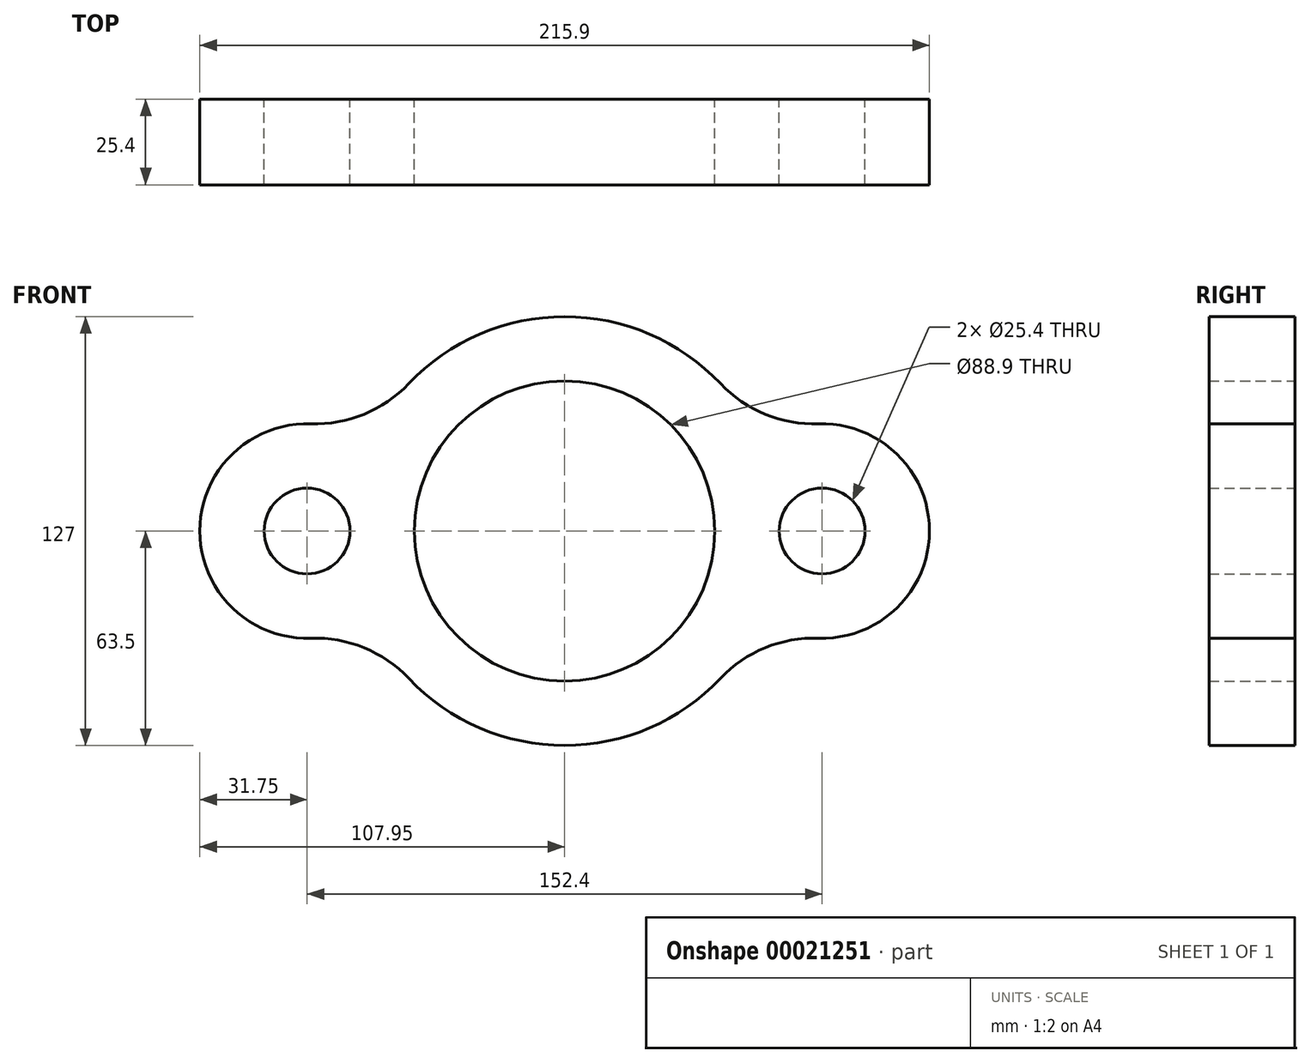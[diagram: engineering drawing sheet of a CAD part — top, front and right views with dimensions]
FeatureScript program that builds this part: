
annotation { "Feature Type Name" : "Feature", "Feature Type Description" : "" }
export const myFeature = defineFeature(function(context is Context, id is Id, definition is map)
    precondition{}
    {
        {
            var Q0;
            Q0=qCreatedBy(makeId("Front.planeOp"),FACE);
            var sketch = newSketch(context, id + "F0", { "sketchPlane" : qUnion([Q0])});
            skCircle(sketch, "E0", {"center": v(0, 0) * mm, "radius": 44.45 * mm});
            skArc(sketch, "E1", {"start": v(-75.12, 31.73) * mm, "mid": v(-107.95, 0) * mm, "end": v(-75.12, -31.73) * mm});
            skArc(sketch, "E2", {"start": v(75.12, -31.73) * mm, "mid": v(107.95, 0) * mm, "end": v(75.12, 31.73) * mm});
            skCircle(sketch, "E3", {"center": v(-76.2, 0) * mm, "radius": 12.7 * mm});
            skCircle(sketch, "E4", {"center": v(76.2, 0) * mm, "radius": 12.7 * mm});
            skArc(sketch, "E5", {"start": v(-46.14, -43.63) * mm, "mid": v(0, -63.5) * mm, "end": v(46.14, -43.63) * mm});
            skArc(sketch, "E6.trimOffspring", {"start": v(46.14, 43.63) * mm, "mid": v(0, 63.5) * mm, "end": v(-46.14, 43.63) * mm});
            skArc(sketch, "E7.filletArc", {"start": v(-75.12, 31.73) * mm, "mid": v(-59.35, 34.56) * mm, "end": v(-46.14, 43.63) * mm});
            skArc(sketch, "E8.filletArc", {"start": v(-46.14, -43.63) * mm, "mid": v(-59.35, -34.56) * mm, "end": v(-75.12, -31.73) * mm});
            skArc(sketch, "E9.filletArc", {"start": v(46.14, 43.63) * mm, "mid": v(59.35, 34.56) * mm, "end": v(75.12, 31.73) * mm});
            skArc(sketch, "E10.filletArc", {"start": v(75.12, -31.73) * mm, "mid": v(59.35, -34.56) * mm, "end": v(46.14, -43.63) * mm});
            skSolve(sketch);
        }
        {
            var Q0;
            Q0 = qSketchRegion(id + "F0", true);
            extrude(context, id + "F1", {"entities" : qUnion([Q0]), "depth" : 25.4 * mm});
        }
    });
